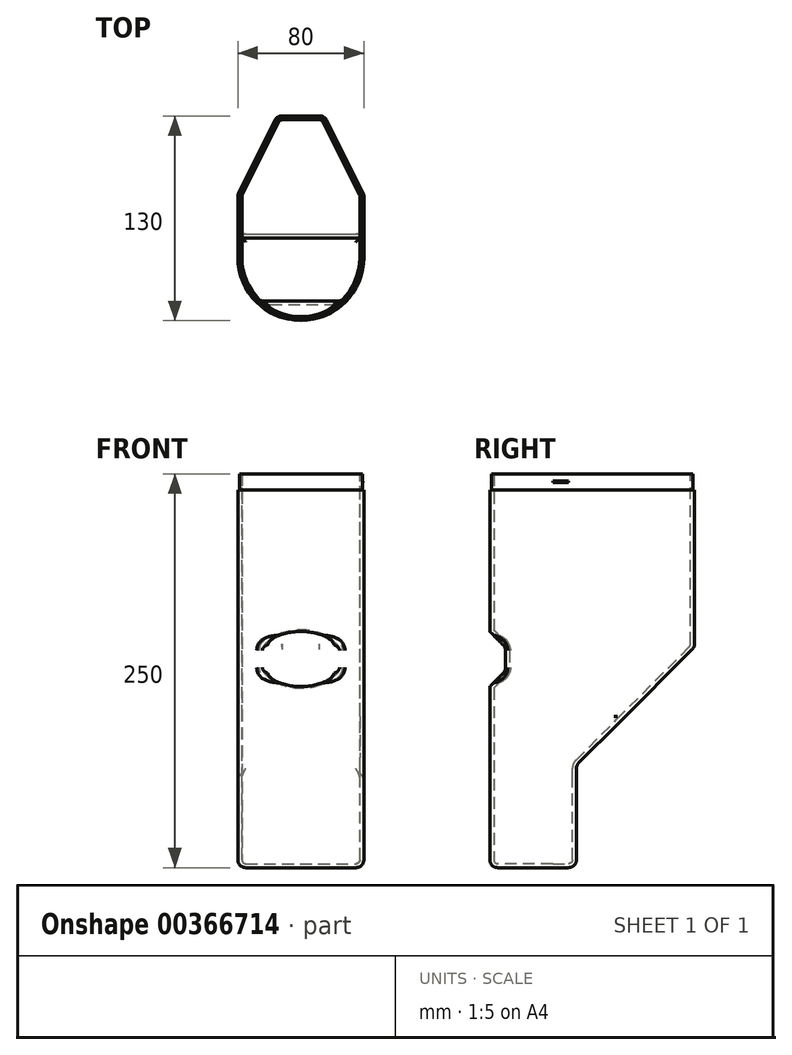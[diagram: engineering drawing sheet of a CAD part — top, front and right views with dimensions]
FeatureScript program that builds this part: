
annotation { "Feature Type Name" : "Feature", "Feature Type Description" : "" }
export const myFeature = defineFeature(function(context is Context, id is Id, definition is map)
    precondition{}
    {
        {
            var Q0;
            Q0=qCreatedBy(makeId("Top.planeOp"),FACE);
            var sketch = newSketch(context, id + "F0", { "sketchPlane" : qUnion([Q0])});
            skArc(sketch, "E0", {"start": v(-40, 0) * mm, "mid": v(0, -40) * mm, "end": v(40, 0) * mm});
            skLineSegment(sketch, "E1", {"start": v(-15, 90) * mm, "end": v(15, 90) * mm});
            skLineSegment(sketch, "E2", {"start": v(-40, 0) * mm, "end": v(-40, 40) * mm});
            skLineSegment(sketch, "E3", {"start": v(-40, 40) * mm, "end": v(-15, 90) * mm});
            skLineSegment(sketch, "E4", {"start": v(40, 0) * mm, "end": v(40, 40) * mm});
            skLineSegment(sketch, "E5", {"start": v(40, 40) * mm, "end": v(15, 90) * mm});
            skSolve(sketch);
        }
        {
            var Q0;
            Q0=makeQuery(id+"F0.imprint","IMPRINT",FACE,{"disambiguationData":[TD([[makeQuery(id+"F0.imprint","IMPRINT",EDGE,{"derivedFrom":sQuery(id+"F0.wireOp",EDGE,"E0")}),1.0]])]});
            extrude(context, id + "F1", {"entities" : qUnion([Q0]), "depth" : 250 * mm});
        }
        {
            var Q0;
            Q0=qCreatedBy(makeId("Right.planeOp"),FACE);
            var sketch = newSketch(context, id + "F2", { "sketchPlane" : qUnion([Q0])});
            skLineSegment(sketch, "E6.bottom", {"start": v(90, 0) * mm, "end": v(15, 0) * mm});
            skLineSegment(sketch, "E6.left", {"start": v(90, 0) * mm, "end": v(90, 65) * mm});
            skLineSegment(sketch, "E6.right", {"start": v(15, 0) * mm, "end": v(15, 65) * mm});
            skLineSegment(sketch, "E7", {"start": v(15, 65) * mm, "end": v(90, 140) * mm});
            skLineSegment(sketch, "E8", {"start": v(90, 140) * mm, "end": v(90, 65) * mm});
            skSolve(sketch);
        }
        {
            var Q0;
            Q0 = qSketchRegion(id + "F2", true);
            extrude(context, id + "F3", {"entities" : qUnion([Q0]), "operationType" : NewBodyOperationType.REMOVE, "endBound" : BoundingType.SYMMETRIC, "oppositeDirection" : true, "depth" : 80 * mm});
        }
        {
            var Q0;
            Q0=makeQuery(id+"F1.opExtrude","CAP_FACE",FACE,{"disambiguationData":[OSD([sQuery(id+"F0.wireOp",EDGE,"E0"),sQuery(id+"F0.wireOp",EDGE,"E1"),sQuery(id+"F0.wireOp",EDGE,"E2"),sQuery(id+"F0.wireOp",EDGE,"E3"),sQuery(id+"F0.wireOp",EDGE,"E4"),sQuery(id+"F0.wireOp",EDGE,"E5")])],"isStart":true});
            var Q1;
            Q1=makeQuery(id+"F3.boolean.opBoolean","COPY",FACE,{"derivedFrom":makeQuery(id+"F3.opExtrude","SWEPT_FACE",FACE,{"disambiguationData":[OSD([sQuery(id+"F2.wireOp",EDGE,"E7")])]})});
            var Q2;
            Q2=makeQuery(id+"F1.opExtrude","SWEPT_EDGE",EDGE,{"disambiguationData":[OSD([sQuery(id+"F0.wireOp",EDGE,"E4"),sQuery(id+"F0.wireOp",EDGE,"E5")])]});
            var Q3;
            Q3=makeQuery(id+"F1.opExtrude","SWEPT_EDGE",EDGE,{"disambiguationData":[OSD([sQuery(id+"F0.wireOp",EDGE,"E1"),sQuery(id+"F0.wireOp",EDGE,"E5")])]});
            var Q4;
            Q4=makeQuery(id+"F1.opExtrude","SWEPT_EDGE",EDGE,{"disambiguationData":[OSD([sQuery(id+"F0.wireOp",EDGE,"E1"),sQuery(id+"F0.wireOp",EDGE,"E3")])]});
            var Q5;
            Q5=makeQuery(id+"F1.opExtrude","SWEPT_EDGE",EDGE,{"disambiguationData":[OSD([sQuery(id+"F0.wireOp",EDGE,"E2"),sQuery(id+"F0.wireOp",EDGE,"E3")])]});
            fillet(context, id + "F4", {"entities" : qUnion([Q0, Q1, Q2, Q3, Q4, Q5]), "radius" : 5 * mm, "tangentPropagation" : true, "allowEdgeOverflow" : false});
        }
        {
            var Q0;
            Q0=qCreatedBy(makeId("Right.planeOp"),FACE);
            var sketch = newSketch(context, id + "F5", { "sketchPlane" : qUnion([Q0])});
            skLineSegment(sketch, "E9", {"start": v(-40, 115) * mm, "end": v(-30, 125) * mm});
            skLineSegment(sketch, "E10", {"start": v(-30, 125) * mm, "end": v(-30, 140) * mm});
            skLineSegment(sketch, "E11", {"start": v(-30, 140) * mm, "end": v(-40, 150) * mm});
            skLineSegment(sketch, "E12", {"start": v(-40, 150) * mm, "end": v(-40, 115) * mm});
            skSolve(sketch);
        }
        {
            var Q0;
            Q0 = qSketchRegion(id + "F5", true);
            extrude(context, id + "F6", {"entities" : qUnion([Q0]), "operationType" : NewBodyOperationType.REMOVE, "endBound" : BoundingType.SYMMETRIC, "depth" : 85.2 * mm});
        }
        {
            var Q0;
            Q0=makeQuery(id+"F6.boolean.opBoolean","COPY",FACE,{"derivedFrom":makeQuery(id+"F6.opExtrude","SWEPT_FACE",FACE,{"disambiguationData":[OSD([sQuery(id+"F5.wireOp",EDGE,"E10")])]})});
            fillet(context, id + "F7", {"entities" : qUnion([Q0]), "radius" : 5 * mm, "tangentPropagation" : true, "allowEdgeOverflow" : false});
        }
        {
            var Q0;
            Q0=makeQuery(id+"F1.opExtrude","CAP_FACE",FACE,{"disambiguationData":[OSD([sQuery(id+"F0.wireOp",EDGE,"E0"),sQuery(id+"F0.wireOp",EDGE,"E1"),sQuery(id+"F0.wireOp",EDGE,"E2"),sQuery(id+"F0.wireOp",EDGE,"E3"),sQuery(id+"F0.wireOp",EDGE,"E4"),sQuery(id+"F0.wireOp",EDGE,"E5")])],"isStart":false});
            shell(context, id + "F8", {"entities" : qUnion([Q0]), "thickness" : 2.5 * mm});
        }
        {
            var Q0;
            Q0=makeQuery(id+"F1.opExtrude","CAP_FACE",FACE,{"disambiguationData":[OSD([sQuery(id+"F0.wireOp",EDGE,"E0"),sQuery(id+"F0.wireOp",EDGE,"E1"),sQuery(id+"F0.wireOp",EDGE,"E2"),sQuery(id+"F0.wireOp",EDGE,"E3"),sQuery(id+"F0.wireOp",EDGE,"E4"),sQuery(id+"F0.wireOp",EDGE,"E5")])],"isStart":false});
            var sketch = newSketch(context, id + "F9", { "sketchPlane" : qUnion([Q0])});
            skLineSegment(sketch, "E13.0", {"start": v(-11.9, 89) * mm, "end": v(11.9, 89) * mm});
            skArc(sketch, "E13.1", {"start": v(15.49, 86.79) * mm, "mid": v(14.01, 88.4) * mm, "end": v(11.9, 89) * mm});
            skArc(sketch, "E13.2", {"start": v(-11.9, 89) * mm, "mid": v(-14.01, 88.4) * mm, "end": v(-15.49, 86.79) * mm});
            skLineSegment(sketch, "E13.3", {"start": v(38.58, 40.6) * mm, "end": v(15.49, 86.79) * mm});
            skArc(sketch, "E13.4", {"start": v(39, 38.82) * mm, "mid": v(38.9, 39.74) * mm, "end": v(38.58, 40.6) * mm});
            skLineSegment(sketch, "E13.5", {"start": v(39, 0) * mm, "end": v(39, 38.82) * mm});
            skLineSegment(sketch, "E13.6", {"start": v(-38.58, 40.6) * mm, "end": v(-15.49, 86.79) * mm});
            skArc(sketch, "E13.7", {"start": v(-38.58, 40.6) * mm, "mid": v(-38.9, 39.74) * mm, "end": v(-39, 38.82) * mm});
            skLineSegment(sketch, "E13.8", {"start": v(-39, 0) * mm, "end": v(-39, 38.82) * mm});
            skArc(sketch, "E13.9", {"start": v(-39, 0) * mm, "mid": v(0, -39) * mm, "end": v(39, 0) * mm});
            skLineSegment(sketch, "E14.0", {"start": v(-11.9, 90) * mm, "end": v(11.9, 90) * mm});
            skArc(sketch, "E14.1", {"start": v(16.38, 87.24) * mm, "mid": v(14.54, 89.25) * mm, "end": v(11.9, 90) * mm});
            skArc(sketch, "E14.2", {"start": v(-11.9, 90) * mm, "mid": v(-14.54, 89.25) * mm, "end": v(-16.38, 87.24) * mm});
            skLineSegment(sketch, "E14.3", {"start": v(39.47, 41.06) * mm, "end": v(16.38, 87.24) * mm});
            skArc(sketch, "E14.4", {"start": v(40, 38.82) * mm, "mid": v(39.87, 39.97) * mm, "end": v(39.47, 41.06) * mm});
            skLineSegment(sketch, "E14.5", {"start": v(40, 0) * mm, "end": v(40, 38.82) * mm});
            skLineSegment(sketch, "E14.6", {"start": v(-39.47, 41.06) * mm, "end": v(-16.38, 87.24) * mm});
            skArc(sketch, "E14.7", {"start": v(-39.47, 41.06) * mm, "mid": v(-39.87, 39.97) * mm, "end": v(-40, 38.82) * mm});
            skLineSegment(sketch, "E14.8", {"start": v(-40, 0) * mm, "end": v(-40, 38.82) * mm});
            skArc(sketch, "E14.9", {"start": v(-40, 0) * mm, "mid": v(0, -40) * mm, "end": v(40, 0) * mm});
            skSolve(sketch);
        }
        {
            var Q0;
            Q0 = qSketchRegion(id + "F9", true);
            extrude(context, id + "F10", {"entities" : qUnion([Q0]), "operationType" : NewBodyOperationType.REMOVE, "oppositeDirection" : true, "depth" : 10 * mm});
        }
        {
            var Q0;
            Q0=qCreatedBy(makeId("Front.planeOp"),FACE);
            var sketch = newSketch(context, id + "F11", { "sketchPlane" : qUnion([Q0])});
            skCircle(sketch, "E15", {"center": v(39, 245) * mm, "radius": 0.5 * mm});
            skSolve(sketch);
        }
        {
            var Q0;
            Q0 = qSketchRegion(id + "F11", true);
            extrude(context, id + "F12", {"entities" : qUnion([Q0]), "operationType" : NewBodyOperationType.ADD, "oppositeDirection" : true, "depth" : 10 * mm});
        }
    });
